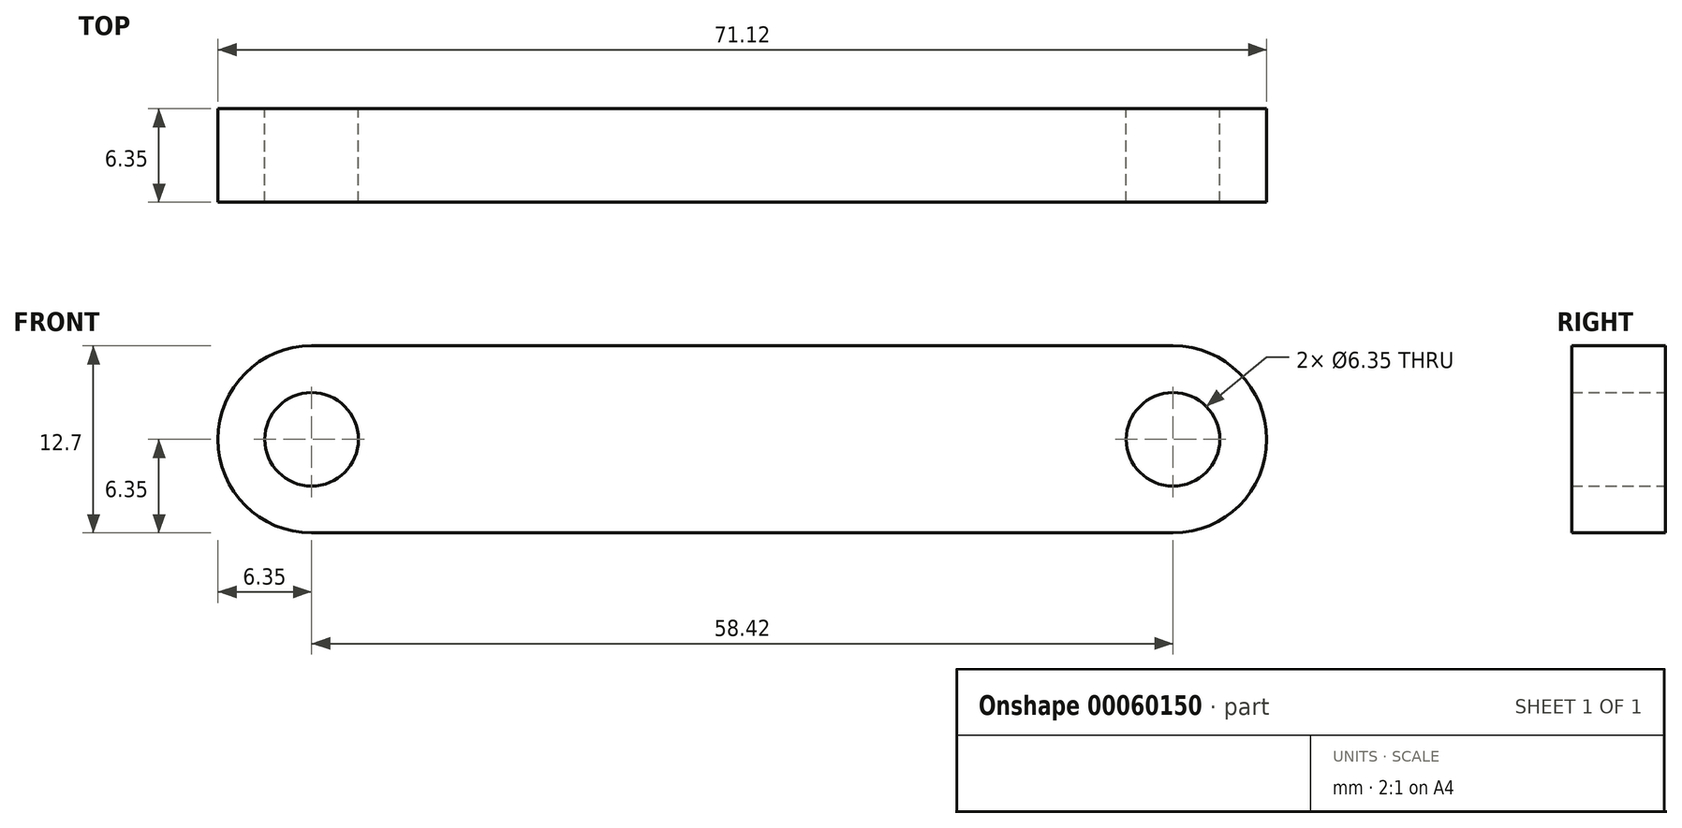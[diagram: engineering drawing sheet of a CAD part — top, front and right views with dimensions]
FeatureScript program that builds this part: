
annotation { "Feature Type Name" : "Feature", "Feature Type Description" : "" }
export const myFeature = defineFeature(function(context is Context, id is Id, definition is map)
    precondition{}
    {
        {
            var Q0;
            Q0=qCreatedBy(makeId("Front.planeOp"),FACE);
            var sketch = newSketch(context, id + "F0", { "sketchPlane" : qUnion([Q0])});
            skLineSegment(sketch, "E0.bottom", {"start": v(-29.21, 6.35) * mm, "end": v(29.21, 6.35) * mm});
            skLineSegment(sketch, "E0.top", {"start": v(-29.21, -6.35) * mm, "end": v(29.21, -6.35) * mm});
            skLineSegment(sketch, "E0.left", {"start": v(-29.21, 6.35) * mm, "end": v(-29.21, -6.35) * mm});
            skLineSegment(sketch, "E0.right", {"start": v(29.21, 6.35) * mm, "end": v(29.21, -6.35) * mm});
            skCircle(sketch, "E1", {"center": v(-29.21, 0) * mm, "radius": 6.35 * mm});
            skCircle(sketch, "E2", {"center": v(29.21, 0) * mm, "radius": 6.35 * mm});
            skCircle(sketch, "E3", {"center": v(-29.21, 0) * mm, "radius": 3.18 * mm});
            skCircle(sketch, "E4", {"center": v(29.21, 0) * mm, "radius": 3.18 * mm});
            skSolve(sketch);
        }
        {
            var Q0;
            {var subQ0=sQuery(id+"F0.wireOp",EDGE,"E0.bottom");Q0=makeQuery(id+"F0.imprint","IMPRINT",FACE,{"disambiguationData":[TD([[makeQuery(id+"F0.imprint","IMPRINT",EDGE,{"derivedFrom":subQ0}),-1.0]])]});}
            var Q1;
            {var subQ1=sQuery(id+"F0.wireOp",EDGE,"E0.left");var subQ3=sQuery(id+"F0.wireOp",EDGE,"E3");var subQ4=makeQuery(id+"F0.imprint","INTERSECT",VERTEX,{"disambiguationData":[OD(0.0)],"derivedFrom":[subQ1,subQ3]});Q1=makeQuery(id+"F0.imprint","IMPRINT",FACE,{"disambiguationData":[TD([[makeQuery(id+"F0.imprint","IMPRINT",EDGE,{"disambiguationData":[TD([[subQ4,1.0]])],"derivedFrom":subQ3}),-1.0]])]});}
            var Q2;
            {var subQ1=sQuery(id+"F0.wireOp",EDGE,"E0.left");var subQ3=sQuery(id+"F0.wireOp",EDGE,"E3");var subQ4=makeQuery(id+"F0.imprint","INTERSECT",VERTEX,{"disambiguationData":[OD(0.0)],"derivedFrom":[subQ1,subQ3]});Q2=makeQuery(id+"F0.imprint","IMPRINT",FACE,{"disambiguationData":[TD([[makeQuery(id+"F0.imprint","IMPRINT",EDGE,{"disambiguationData":[TD([[subQ4,-1.0]])],"derivedFrom":subQ3}),-1.0]])]});}
            var Q3;
            {var subQ1=sQuery(id+"F0.wireOp",EDGE,"E0.right");var subQ3=sQuery(id+"F0.wireOp",EDGE,"E4");var subQ4=makeQuery(id+"F0.imprint","INTERSECT",VERTEX,{"disambiguationData":[OD(0.0)],"derivedFrom":[subQ1,subQ3]});Q3=makeQuery(id+"F0.imprint","IMPRINT",FACE,{"disambiguationData":[TD([[makeQuery(id+"F0.imprint","IMPRINT",EDGE,{"disambiguationData":[TD([[subQ4,-1.0]])],"derivedFrom":subQ3}),-1.0]])]});}
            var Q4;
            {var subQ1=sQuery(id+"F0.wireOp",EDGE,"E0.right");var subQ3=sQuery(id+"F0.wireOp",EDGE,"E4");var subQ4=makeQuery(id+"F0.imprint","INTERSECT",VERTEX,{"disambiguationData":[OD(0.0)],"derivedFrom":[subQ1,subQ3]});Q4=makeQuery(id+"F0.imprint","IMPRINT",FACE,{"disambiguationData":[TD([[makeQuery(id+"F0.imprint","IMPRINT",EDGE,{"disambiguationData":[TD([[subQ4,1.0]])],"derivedFrom":subQ3}),-1.0]])]});}
            extrude(context, id + "F1", {"entities" : qUnion([Q0, Q1, Q2, Q3, Q4]), "depth" : 6.35 * mm});
        }
    });
